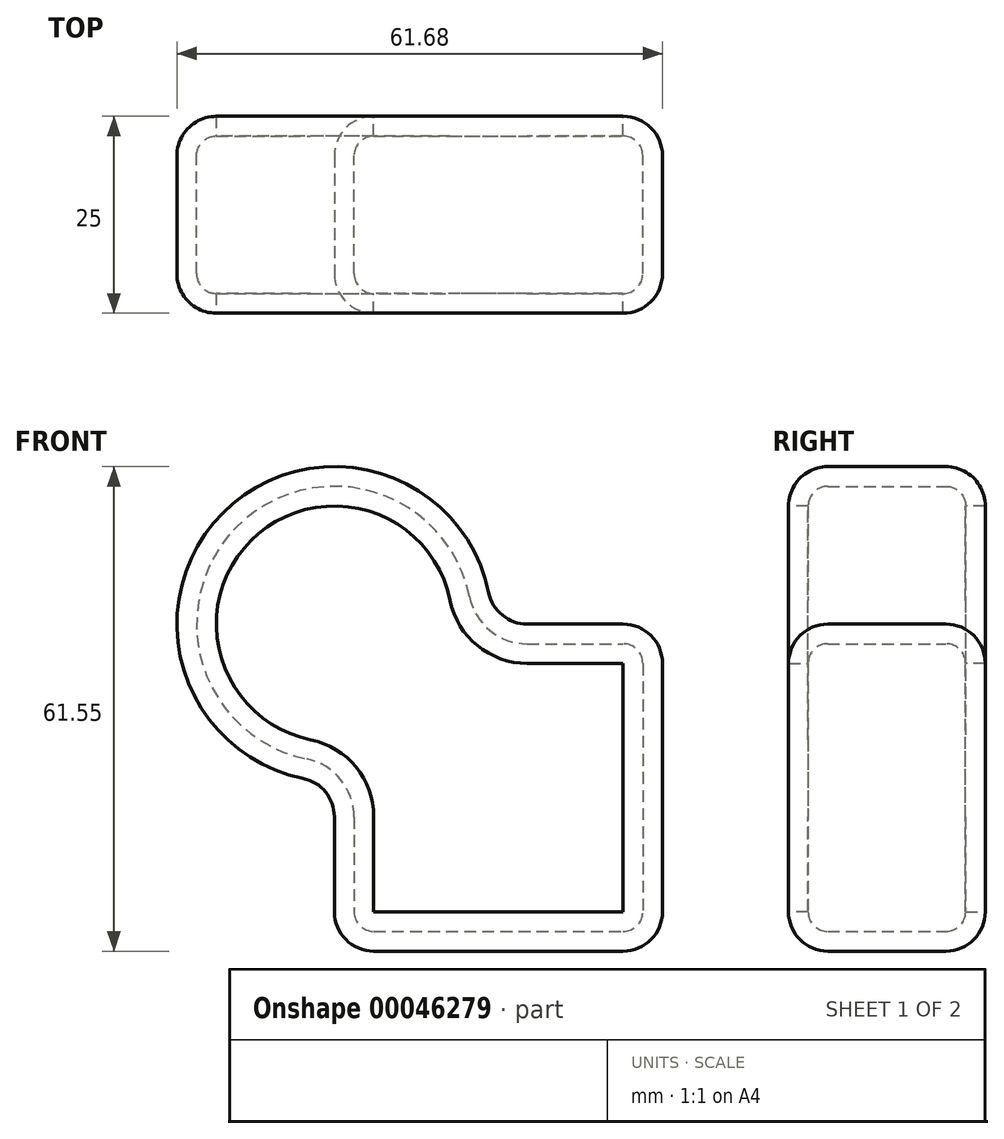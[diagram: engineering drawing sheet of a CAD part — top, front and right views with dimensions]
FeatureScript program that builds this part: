
annotation { "Feature Type Name" : "Feature", "Feature Type Description" : "" }
export const myFeature = defineFeature(function(context is Context, id is Id, definition is map)
    precondition{}
    {
        {
            var Q0;
            Q0=qCreatedBy(makeId("Front.planeOp"),FACE);
            var sketch = newSketch(context, id + "F0", { "sketchPlane" : qUnion([Q0])});
            skCircle(sketch, "E0", {"center": v(0, 0) * mm, "radius": 20 * mm});
            skLineSegment(sketch, "E1.bottom", {"start": v(0, 0) * mm, "end": v(41.68, 0) * mm});
            skLineSegment(sketch, "E1.top", {"start": v(0, -41.55) * mm, "end": v(41.68, -41.55) * mm});
            skLineSegment(sketch, "E1.left", {"start": v(0, 0) * mm, "end": v(0, -41.55) * mm});
            skLineSegment(sketch, "E1.right", {"start": v(41.68, 0) * mm, "end": v(41.68, -41.55) * mm});
            skSolve(sketch);
        }
        {
            var Q0;
            {var subQ1=sQuery(id+"F0.wireOp",EDGE,"E0");var subQ3=sQuery(id+"F0.wireOp",EDGE,"E1.bottom");var subQ5=makeQuery(id+"F0.imprint","INTERSECT",VERTEX,{"derivedFrom":[subQ1,subQ3]});Q0=makeQuery(id+"F0.imprint","IMPRINT",FACE,{"disambiguationData":[TD([[makeQuery(id+"F0.imprint","IMPRINT",EDGE,{"disambiguationData":[TD([[subQ5,1.0]])],"derivedFrom":subQ1}),1.0]])]});}
            var Q1;
            {var subQ6=sQuery(id+"F0.wireOp",EDGE,"E1.top");Q1=makeQuery(id+"F0.imprint","IMPRINT",FACE,{"disambiguationData":[TD([[makeQuery(id+"F0.imprint","IMPRINT",EDGE,{"derivedFrom":subQ6}),1.0]])]});}
            var Q2;
            {var subQ1=sQuery(id+"F0.wireOp",EDGE,"E0");var subQ3=sQuery(id+"F0.wireOp",EDGE,"E1.bottom");var subQ5=makeQuery(id+"F0.imprint","INTERSECT",VERTEX,{"derivedFrom":[subQ1,subQ3]});Q2=makeQuery(id+"F0.imprint","IMPRINT",FACE,{"disambiguationData":[TD([[makeQuery(id+"F0.imprint","IMPRINT",EDGE,{"disambiguationData":[TD([[subQ5,-1.0]])],"derivedFrom":subQ1}),1.0]])]});}
            extrude(context, id + "F1", {"entities" : qUnion([Q0, Q1, Q2]), "depth" : 25 * mm});
        }
        {
            var Q0;
            Q0=makeQuery(id+"F1.opExtrude","CAP_EDGE",EDGE,{"disambiguationData":[OSD([sQuery(id+"F0.wireOp",EDGE,"E1.bottom")])],"isStart":false});
            var Q1;
            Q1=makeQuery(id+"F1.opExtrude","CAP_EDGE",EDGE,{"disambiguationData":[OSD([sQuery(id+"F0.wireOp",EDGE,"E1.bottom")])],"isStart":true});
            var Q2;
            Q2=makeQuery(id+"F1.opExtrude","SWEPT_EDGE",EDGE,{"disambiguationData":[OSD([sQuery(id+"F0.wireOp",EDGE,"E1.bottom"),sQuery(id+"F0.wireOp",EDGE,"E1.right")])]});
            var Q3;
            Q3=makeQuery(id+"F1.opExtrude","SWEPT_EDGE",EDGE,{"disambiguationData":[OSD([sQuery(id+"F0.wireOp",EDGE,"E1.top"),sQuery(id+"F0.wireOp",EDGE,"E1.right")])]});
            var Q4;
            Q4=makeQuery(id+"F1.opExtrude","CAP_EDGE",EDGE,{"disambiguationData":[OSD([sQuery(id+"F0.wireOp",EDGE,"E1.right")])],"isStart":true});
            var Q5;
            Q5=makeQuery(id+"F1.opExtrude","CAP_EDGE",EDGE,{"disambiguationData":[OSD([sQuery(id+"F0.wireOp",EDGE,"E1.right")])],"isStart":false});
            var Q6;
            Q6=makeQuery(id+"F1.opExtrude","CAP_EDGE",EDGE,{"disambiguationData":[OSD([sQuery(id+"F0.wireOp",EDGE,"E1.left")])],"isStart":true});
            var Q7;
            Q7=makeQuery(id+"F1.opExtrude","SWEPT_EDGE",EDGE,{"disambiguationData":[OSD([sQuery(id+"F0.wireOp",EDGE,"E1.top"),sQuery(id+"F0.wireOp",EDGE,"E1.left")])]});
            var Q8;
            Q8=makeQuery(id+"F1.opExtrude","CAP_EDGE",EDGE,{"disambiguationData":[OSD([sQuery(id+"F0.wireOp",EDGE,"E1.top")])],"isStart":true});
            var Q9;
            Q9=makeQuery(id+"F1.opExtrude","CAP_EDGE",EDGE,{"disambiguationData":[OSD([sQuery(id+"F0.wireOp",EDGE,"E1.left")])],"isStart":false});
            var Q10;
            Q10=makeQuery(id+"F1.opExtrude","CAP_EDGE",EDGE,{"disambiguationData":[OSD([sQuery(id+"F0.wireOp",EDGE,"E1.top")])],"isStart":false});
            var Q11;
            Q11=makeQuery(id+"F1.opExtrude","CAP_EDGE",EDGE,{"disambiguationData":[OSD([sQuery(id+"F0.wireOp",EDGE,"E0")])],"isStart":false});
            var Q12;
            Q12=makeQuery(id+"F1.opExtrude","SWEPT_FACE",FACE,{"disambiguationData":[OSD([sQuery(id+"F0.wireOp",EDGE,"E0")])]});
            var Q13;
            Q13=makeQuery(id+"F1.opExtrude","CAP_FACE",FACE,{"disambiguationData":[OSD([sQuery(id+"F0.wireOp",EDGE,"E0"),sQuery(id+"F0.wireOp",EDGE,"E1.bottom"),sQuery(id+"F0.wireOp",EDGE,"E1.top"),sQuery(id+"F0.wireOp",EDGE,"E1.left"),sQuery(id+"F0.wireOp",EDGE,"E1.right")])],"isStart":false});
            fillet(context, id + "F2", {"entities" : qUnion([Q0, Q1, Q2, Q3, Q4, Q5, Q6, Q7, Q8, Q9, Q10, Q11, Q12, Q13]), "radius" : 5 * mm, "tangentPropagation" : true, "allowEdgeOverflow" : false});
        }
        {
            var Q0;
            Q0=makeQuery(id+"F1.opExtrude","CAP_FACE",FACE,{"disambiguationData":[OSD([sQuery(id+"F0.wireOp",EDGE,"E0"),sQuery(id+"F0.wireOp",EDGE,"E1.bottom"),sQuery(id+"F0.wireOp",EDGE,"E1.top"),sQuery(id+"F0.wireOp",EDGE,"E1.left"),sQuery(id+"F0.wireOp",EDGE,"E1.right")])],"isStart":false});
            var Q1;
            Q1=makeQuery(id+"F1.opExtrude","CAP_FACE",FACE,{"disambiguationData":[OSD([sQuery(id+"F0.wireOp",EDGE,"E0"),sQuery(id+"F0.wireOp",EDGE,"E1.bottom"),sQuery(id+"F0.wireOp",EDGE,"E1.top"),sQuery(id+"F0.wireOp",EDGE,"E1.left"),sQuery(id+"F0.wireOp",EDGE,"E1.right")])],"isStart":true});
            shell(context, id + "F3", {"entities" : qUnion([Q0, Q1]), "thickness" : 2.5 * mm});
        }
    });
